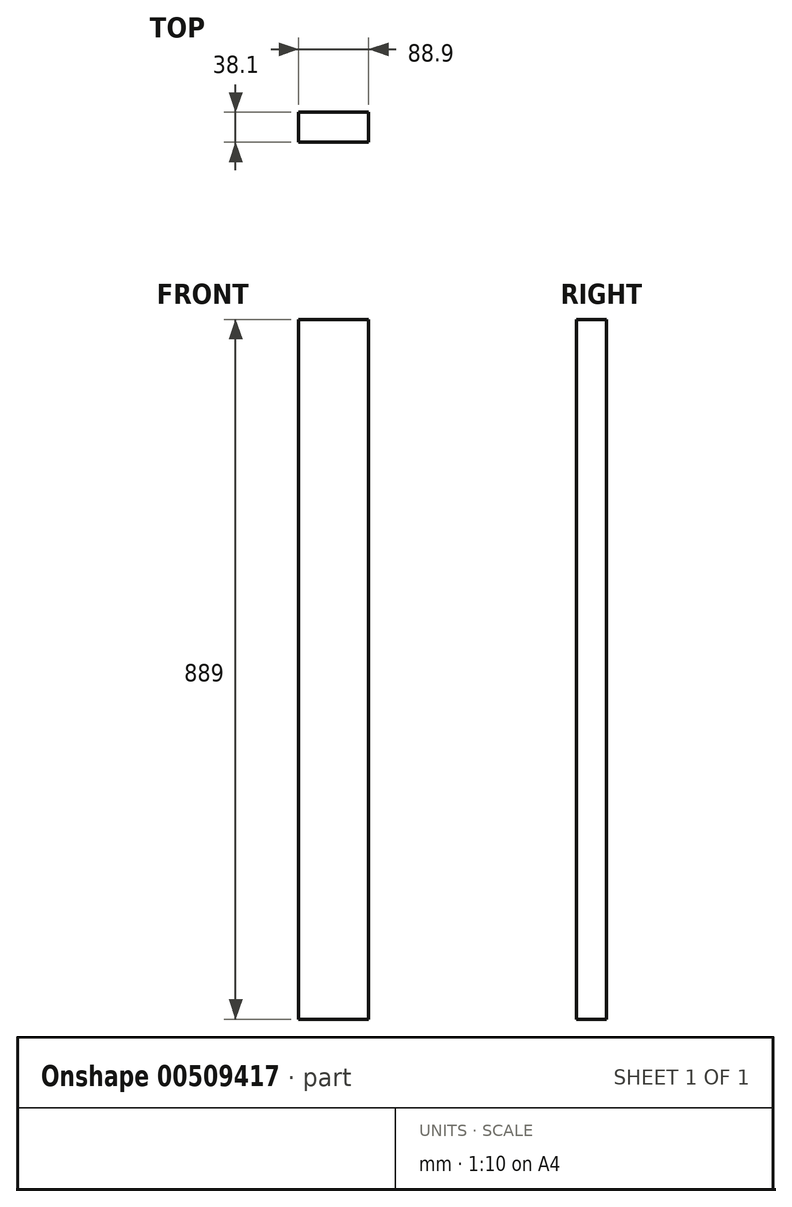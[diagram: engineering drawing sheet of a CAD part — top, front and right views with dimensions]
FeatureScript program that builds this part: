
annotation { "Feature Type Name" : "Feature", "Feature Type Description" : "" }
export const myFeature = defineFeature(function(context is Context, id is Id, definition is map)
    precondition{}
    {
        {
            var Q0;
            Q0=qCreatedBy(makeId("Top.planeOp"),FACE);
            var sketch = newSketch(context, id + "F0", { "sketchPlane" : qUnion([Q0])});
            skLineSegment(sketch, "E0.bottom", {"start": v(-44.45, 19.05) * mm, "end": v(44.45, 19.05) * mm});
            skLineSegment(sketch, "E0.top", {"start": v(-44.45, -19.05) * mm, "end": v(44.45, -19.05) * mm});
            skLineSegment(sketch, "E0.left", {"start": v(-44.45, 19.05) * mm, "end": v(-44.45, -19.05) * mm});
            skLineSegment(sketch, "E0.right", {"start": v(44.45, 19.05) * mm, "end": v(44.45, -19.05) * mm});
            skLineSegment(sketch, "E1", {"start": v(0, 19.05) * mm, "end": v(0, -19.05) * mm, "construction": true});
            skLineSegment(sketch, "E2", {"start": v(-44.45, 0) * mm, "end": v(44.45, 0) * mm, "construction": true});
            skSolve(sketch);
        }
        {
            var Q0;
            Q0 = qSketchRegion(id + "F0", true);
            extrude(context, id + "F1", {"entities" : qUnion([Q0]), "depth" : 889 * mm});
        }
    });
